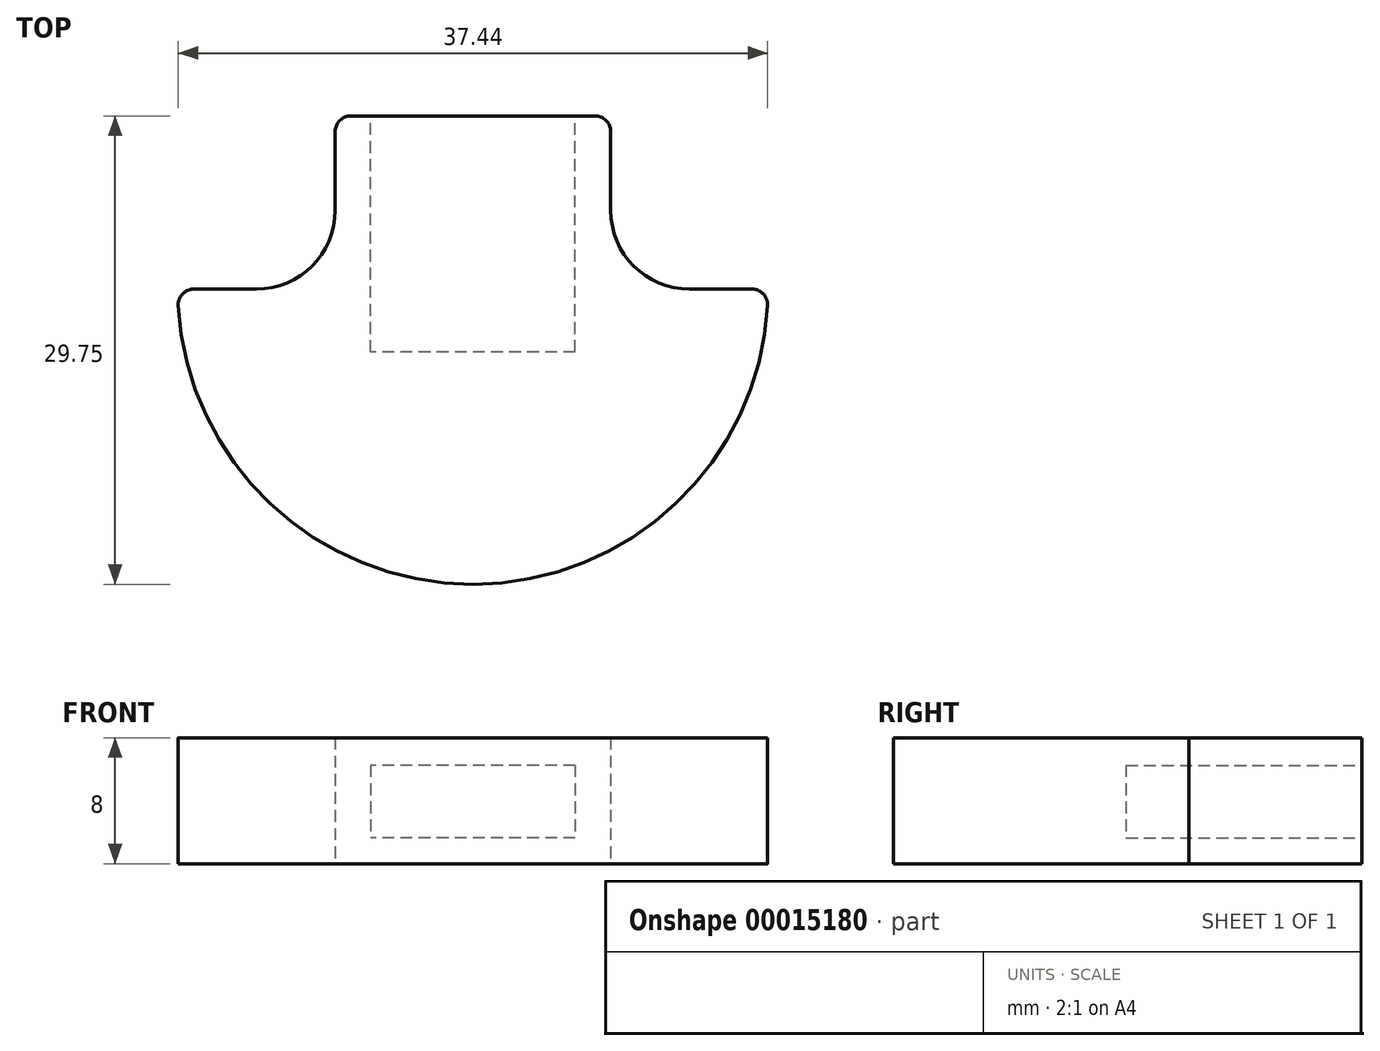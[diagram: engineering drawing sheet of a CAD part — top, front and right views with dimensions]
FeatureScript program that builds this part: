
annotation { "Feature Type Name" : "Feature", "Feature Type Description" : "" }
export const myFeature = defineFeature(function(context is Context, id is Id, definition is map)
    precondition{}
    {
        {
            var Q0;
            Q0=qCreatedBy(makeId("Top.planeOp"),FACE);
            var sketch = newSketch(context, id + "F0", { "sketchPlane" : qUnion([Q0])});
            skLineSegment(sketch, "E0.rect.top", {"start": v(7.75, 5.5) * mm, "end": v(-7.75, 5.5) * mm});
            skLineSegment(sketch, "E0.rect.left", {"start": v(8.75, -0.5) * mm, "end": v(8.75, 4.5) * mm});
            skLineSegment(sketch, "E0.rect.right", {"start": v(-8.75, -0.5) * mm, "end": v(-8.75, 4.5) * mm});
            skPoint(sketch, "E0.rect.middle", {"position": v(0, 0) * mm});
            skLineSegment(sketch, "E1", {"start": v(-13.75, -5.5) * mm, "end": v(-17.72, -5.5) * mm});
            skLineSegment(sketch, "E2", {"start": v(13.75, -5.5) * mm, "end": v(17.72, -5.5) * mm});
            skArc(sketch, "E3", {"start": v(-18.72, -6.56) * mm, "mid": v(0, -24.25) * mm, "end": v(18.72, -6.56) * mm});
            skPoint(sketch, "E4.visualSharp", {"position": v(-8.75, -5.5) * mm});
            skArc(sketch, "E4.filletArc", {"start": v(-13.75, -5.5) * mm, "mid": v(-10.21, -4.04) * mm, "end": v(-8.75, -0.5) * mm});
            skPoint(sketch, "E5.visualSharp", {"position": v(8.75, -5.5) * mm});
            skArc(sketch, "E5.filletArc", {"start": v(8.75, -0.5) * mm, "mid": v(10.21, -4.04) * mm, "end": v(13.75, -5.5) * mm});
            skPoint(sketch, "E6.visualSharp", {"position": v(-8.75, 5.5) * mm});
            skArc(sketch, "E6.filletArc", {"start": v(-7.75, 5.5) * mm, "mid": v(-8.46, 5.2) * mm, "end": v(-8.75, 4.5) * mm});
            skPoint(sketch, "E7.visualSharp", {"position": v(8.75, 5.5) * mm});
            skArc(sketch, "E7.filletArc", {"start": v(8.75, 4.5) * mm, "mid": v(8.46, 5.2) * mm, "end": v(7.75, 5.5) * mm});
            skPoint(sketch, "E8.visualSharp", {"position": v(-18.75, -5.5) * mm});
            skArc(sketch, "E8.filletArc", {"start": v(-17.72, -5.5) * mm, "mid": v(-18.45, -5.81) * mm, "end": v(-18.72, -6.56) * mm});
            skPoint(sketch, "E9.visualSharp", {"position": v(18.75, -5.5) * mm});
            skArc(sketch, "E9.filletArc", {"start": v(18.72, -6.56) * mm, "mid": v(18.45, -5.81) * mm, "end": v(17.72, -5.5) * mm});
            skSolve(sketch);
        }
        {
            var Q0;
            Q0=qSketchRegion(id+"F0",true);
            extrude(context, id + "F1", {"entities" : qUnion([Q0]), "depth" : 8 * mm});
        }
        {
            var Q0;
            Q0=makeQuery(id+"F1.opExtrude","SWEPT_FACE",FACE,{"disambiguationData":[OSD([sQuery(id+"F0.wireOp",EDGE,"E0.rect.top")])]});
            var sketch = newSketch(context, id + "F2", { "sketchPlane" : qUnion([Q0])});
            skLineSegment(sketch, "E10", {"start": v(0, 0) * mm, "end": v(0, 8) * mm});
            skLineSegment(sketch, "E11.rect.bottom", {"start": v(-6.5, 6.25) * mm, "end": v(6.5, 6.25) * mm});
            skLineSegment(sketch, "E11.rect.top", {"start": v(-6.5, 1.65) * mm, "end": v(6.5, 1.65) * mm});
            skLineSegment(sketch, "E11.rect.left", {"start": v(-6.5, 6.25) * mm, "end": v(-6.5, 1.65) * mm});
            skLineSegment(sketch, "E11.rect.right", {"start": v(6.5, 6.25) * mm, "end": v(6.5, 1.65) * mm});
            skPoint(sketch, "E11.rect.middle", {"position": v(0, 3.95) * mm});
            skSolve(sketch);
        }
        {
            var Q0;
            Q0=qSketchRegion(id+"F2",true);
            extrude(context, id + "F3", {"entities" : qUnion([Q0]), "operationType" : NewBodyOperationType.REMOVE, "oppositeDirection" : true, "depth" : 15 * mm});
        }
    });
